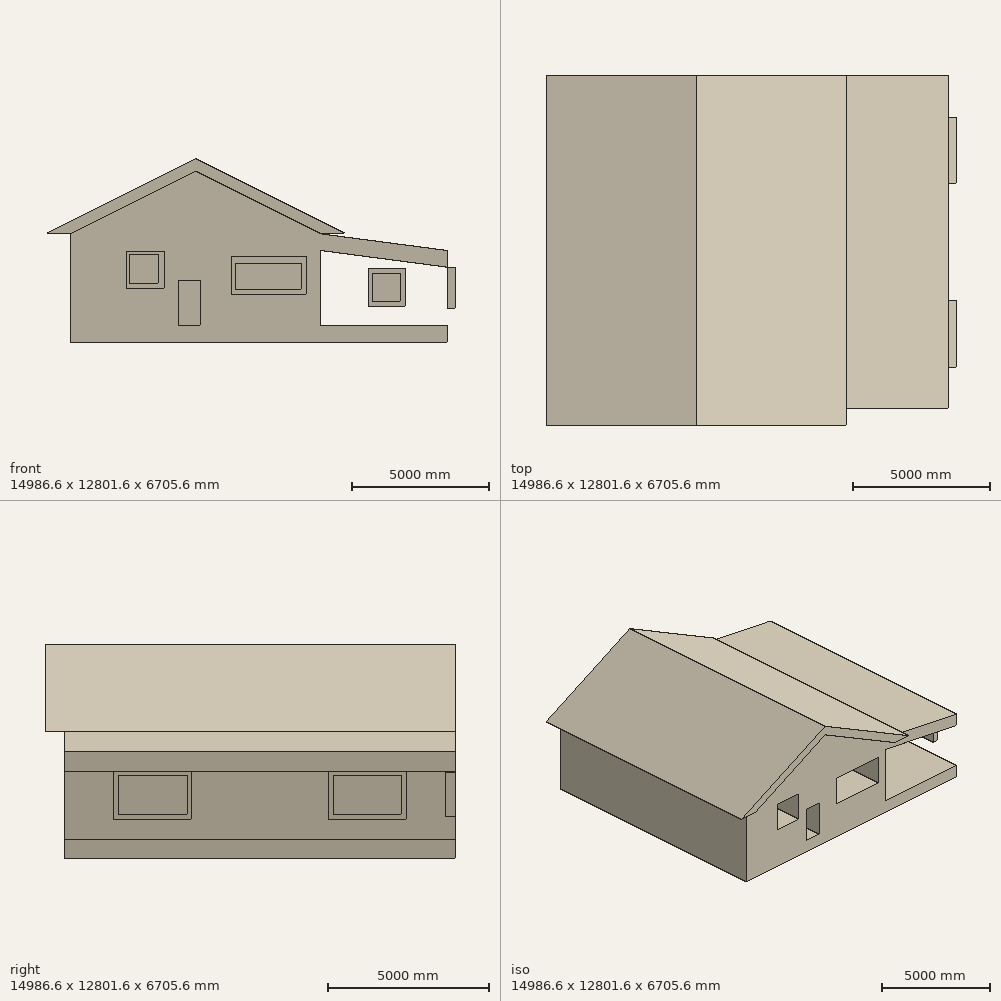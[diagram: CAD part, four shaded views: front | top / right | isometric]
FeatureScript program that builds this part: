
annotation { "Feature Type Name" : "Feature", "Feature Type Description" : "" }
export const myFeature = defineFeature(function(context is Context, id is Id, definition is map)
    precondition{}
    {
        {
            var Q0;
            Q0=qCreatedBy(makeId("Front.planeOp"),FACE);
            var sketch = newSketch(context, id + "F0", { "sketchPlane" : qUnion([Q0])});
            skLineSegment(sketch, "E0", {"start": v(0, 0) * mm, "end": v(0, 2286) * mm});
            skLineSegment(sketch, "E1", {"start": v(0, 0) * mm, "end": v(-4572, 0) * mm});
            skLineSegment(sketch, "E2", {"start": v(0, 0) * mm, "end": v(4572, 0) * mm});
            skLineSegment(sketch, "E3", {"start": v(-4572, 0) * mm, "end": v(0, 2286) * mm});
            skLineSegment(sketch, "E4", {"start": v(4572, 0) * mm, "end": v(0, 2286) * mm});
            skLineSegment(sketch, "E5", {"start": v(-4572, 0) * mm, "end": v(-5486.4, 0) * mm});
            skLineSegment(sketch, "E6", {"start": v(4572, 0) * mm, "end": v(5486.4, 0) * mm});
            skLineSegment(sketch, "E7", {"start": v(-5486.4, 0) * mm, "end": v(0, 2743.2) * mm});
            skLineSegment(sketch, "E8", {"start": v(5486.4, 0) * mm, "end": v(0, 2743.2) * mm});
            skLineSegment(sketch, "E9", {"start": v(0, 2286) * mm, "end": v(0, 2743.2) * mm});
            skLineSegment(sketch, "E10", {"start": v(-4572, 0) * mm, "end": v(-4572, -3352.8) * mm});
            skLineSegment(sketch, "E11", {"start": v(-4572, -3352.8) * mm, "end": v(4623.43, -3352.8) * mm});
            skLineSegment(sketch, "E12", {"start": v(-4572, -3352.8) * mm, "end": v(-4572, -3962.4) * mm});
            skLineSegment(sketch, "E13", {"start": v(-4572, -3962.4) * mm, "end": v(4623.43, -3962.4) * mm});
            skLineSegment(sketch, "E14", {"start": v(4572, 0) * mm, "end": v(4572, -3352.8) * mm});
            skLineSegment(sketch, "E15", {"start": v(4623.43, -3962.4) * mm, "end": v(9195.43, -3962.4) * mm});
            skLineSegment(sketch, "E16", {"start": v(4623.43, -3352.8) * mm, "end": v(9195.43, -3352.8) * mm});
            skLineSegment(sketch, "E17", {"start": v(9195.43, -3352.8) * mm, "end": v(9195.43, -609.6) * mm});
            skLineSegment(sketch, "E18", {"start": v(9195.43, -3352.8) * mm, "end": v(9195.43, -3962.4) * mm});
            skLineSegment(sketch, "E19", {"start": v(4623.43, -3352.8) * mm, "end": v(4623.43, -3962.4) * mm});
            skLineSegment(sketch, "E20", {"start": v(4572, 0) * mm, "end": v(9195.43, -609.6) * mm});
            skLineSegment(sketch, "E21", {"start": v(4572, -609.6) * mm, "end": v(4572, 0) * mm});
            skLineSegment(sketch, "E22", {"start": v(9195.43, -1219.2) * mm, "end": v(9195.43, -609.6) * mm});
            skLineSegment(sketch, "E23", {"start": v(4572, -609.6) * mm, "end": v(9195.43, -1219.2) * mm});
            skLineSegment(sketch, "E24", {"start": v(1327.2, -837.67) * mm, "end": v(1327.2, -2209.27) * mm});
            skLineSegment(sketch, "E25", {"start": v(1327.2, -2209.27) * mm, "end": v(4070.4, -2209.27) * mm});
            skLineSegment(sketch, "E26", {"start": v(4070.4, -2209.27) * mm, "end": v(4070.4, -837.67) * mm});
            skLineSegment(sketch, "E27", {"start": v(4070.4, -837.67) * mm, "end": v(1327.2, -837.67) * mm});
            skLineSegment(sketch, "E28.bottom", {"start": v(-2513.93, -640.84) * mm, "end": v(-1142.33, -640.84) * mm});
            skLineSegment(sketch, "E28.top", {"start": v(-2513.93, -2012.44) * mm, "end": v(-1142.33, -2012.44) * mm});
            skLineSegment(sketch, "E28.left", {"start": v(-2513.93, -640.84) * mm, "end": v(-2513.93, -2012.44) * mm});
            skLineSegment(sketch, "E28.right", {"start": v(-1142.33, -640.84) * mm, "end": v(-1142.33, -2012.44) * mm});
            skLineSegment(sketch, "E29.bottom", {"start": v(-2407.47, -765.33) * mm, "end": v(-1340.67, -765.33) * mm});
            skLineSegment(sketch, "E29.top", {"start": v(-2407.47, -1832.13) * mm, "end": v(-1340.67, -1832.13) * mm});
            skLineSegment(sketch, "E29.left", {"start": v(-2407.47, -765.33) * mm, "end": v(-2407.47, -1832.13) * mm});
            skLineSegment(sketch, "E29.right", {"start": v(-1340.67, -765.33) * mm, "end": v(-1340.67, -1832.13) * mm});
            skLineSegment(sketch, "E30.bottom", {"start": v(1472.1, -1092.88) * mm, "end": v(3888.2, -1092.88) * mm});
            skLineSegment(sketch, "E30.top", {"start": v(1472.1, -2030.47) * mm, "end": v(3888.2, -2030.47) * mm});
            skLineSegment(sketch, "E30.left", {"start": v(1472.1, -1092.88) * mm, "end": v(1472.1, -2030.47) * mm});
            skLineSegment(sketch, "E30.right", {"start": v(3888.2, -1092.88) * mm, "end": v(3888.2, -2030.47) * mm});
            skLineSegment(sketch, "E31.bottom", {"start": v(6303.03, -1271.91) * mm, "end": v(7674.63, -1271.91) * mm});
            skLineSegment(sketch, "E31.top", {"start": v(6303.03, -2643.51) * mm, "end": v(7674.63, -2643.51) * mm});
            skLineSegment(sketch, "E31.left", {"start": v(6303.03, -1271.91) * mm, "end": v(6303.03, -2643.51) * mm});
            skLineSegment(sketch, "E31.right", {"start": v(7674.63, -1271.91) * mm, "end": v(7674.63, -2643.51) * mm});
            skLineSegment(sketch, "E32.bottom", {"start": v(6466.58, -1453.5) * mm, "end": v(7494.32, -1453.5) * mm});
            skLineSegment(sketch, "E32.top", {"start": v(6466.58, -2463.2) * mm, "end": v(7494.32, -2463.2) * mm});
            skLineSegment(sketch, "E32.left", {"start": v(6466.58, -1453.5) * mm, "end": v(6466.58, -2463.2) * mm});
            skLineSegment(sketch, "E32.right", {"start": v(7494.32, -1453.5) * mm, "end": v(7494.32, -2463.2) * mm});
            skLineSegment(sketch, "E33.bottom", {"start": v(-631.5, -1709.5) * mm, "end": v(191.74, -1709.5) * mm});
            skLineSegment(sketch, "E33.top", {"start": v(-631.5, -3352.8) * mm, "end": v(191.74, -3352.8) * mm});
            skLineSegment(sketch, "E33.left", {"start": v(-631.5, -1709.5) * mm, "end": v(-631.5, -3352.8) * mm});
            skLineSegment(sketch, "E33.right", {"start": v(191.74, -1709.5) * mm, "end": v(191.74, -3352.8) * mm});
            skLineSegment(sketch, "E34.bottom", {"start": v(-469.54, -1857.95) * mm, "end": v(25.71, -1857.95) * mm});
            skLineSegment(sketch, "E34.top", {"start": v(-469.54, -3352.8) * mm, "end": v(25.71, -3352.8) * mm});
            skLineSegment(sketch, "E34.left", {"start": v(-469.54, -1857.95) * mm, "end": v(-469.54, -3352.8) * mm});
            skLineSegment(sketch, "E34.right", {"start": v(25.71, -1857.95) * mm, "end": v(25.71, -3352.8) * mm});
            skSolve(sketch);
        }
        {
            var Q0;
            Q0=makeQuery(id+"F0.imprint","IMPRINT",FACE,{"disambiguationData":[TD([[makeQuery(id+"F0.imprint","IMPRINT",EDGE,{"derivedFrom":sQuery(id+"F0.wireOp",EDGE,"E4")}),-1.0]])]});
            var Q1;
            Q1=makeQuery(id+"F0.imprint","IMPRINT",FACE,{"disambiguationData":[TD([[makeQuery(id+"F0.imprint","IMPRINT",EDGE,{"derivedFrom":sQuery(id+"F0.wireOp",EDGE,"E3")}),1.0]])]});
            extrude(context, id + "F1", {"entities" : qUnion([Q0, Q1]), "depth" : 12801.6 * mm, "offsetDistance" : 30.48 * mm});
        }
        {
            var Q0;
            Q0=makeQuery(id+"F0.imprint","IMPRINT",FACE,{"disambiguationData":[TD([[makeQuery(id+"F0.imprint","IMPRINT",EDGE,{"derivedFrom":sQuery(id+"F0.wireOp",EDGE,"E0")}),1.0]])]});
            var Q1;
            Q1=makeQuery(id+"F0.imprint","IMPRINT",FACE,{"disambiguationData":[TD([[makeQuery(id+"F0.imprint","IMPRINT",EDGE,{"derivedFrom":sQuery(id+"F0.wireOp",EDGE,"E0")}),-1.0]])]});
            var Q2;
            Q2=makeQuery(id+"F0.imprint","IMPRINT",FACE,{"disambiguationData":[TD([[makeQuery(id+"F0.imprint","IMPRINT",EDGE,{"derivedFrom":sQuery(id+"F0.wireOp",EDGE,"E1")}),1.0]])]});
            var Q3;
            {var subQ0=sQuery(id+"F0.wireOp",EDGE,"E12");Q3=makeQuery(id+"F0.imprint","IMPRINT",FACE,{"disambiguationData":[TD([[makeQuery(id+"F0.imprint","IMPRINT",EDGE,{"derivedFrom":subQ0}),1.0]])]});}
            var Q4;
            Q4=makeQuery(id+"F0.imprint","IMPRINT",FACE,{"disambiguationData":[TD([[makeQuery(id+"F0.imprint","IMPRINT",EDGE,{"derivedFrom":sQuery(id+"F0.wireOp",EDGE,"E15")}),1.0]])]});
            var Q5;
            {var subQ0=sQuery(id+"F0.wireOp",EDGE,"E14");Q5=makeQuery(id+"F0.imprint","IMPRINT",FACE,{"disambiguationData":[TD([[makeQuery(id+"F0.imprint","IMPRINT",EDGE,{"derivedFrom":subQ0}),1.0]])]});}
            var Q6;
            Q6=makeQuery(id+"F0.imprint","IMPRINT",FACE,{"disambiguationData":[TD([[makeQuery(id+"F0.imprint","IMPRINT",EDGE,{"derivedFrom":sQuery(id+"F0.wireOp",EDGE,"E20")}),-1.0]])]});
            extrude(context, id + "F2", {"entities" : qUnion([Q0, Q1, Q2, Q3, Q4, Q5, Q6]), "operationType" : NewBodyOperationType.ADD, "depth" : 12192 * mm, "offsetDistance" : 30.48 * mm});
        }
        {
            var Q0;
            Q0=makeQuery(id+"F0.imprint","IMPRINT",FACE,{"disambiguationData":[TD([[makeQuery(id+"F0.imprint","IMPRINT",EDGE,{"derivedFrom":sQuery(id+"F0.wireOp",EDGE,"E29.bottom")}),-1.0]])]});
            var Q1;
            Q1=makeQuery(id+"F0.imprint","IMPRINT",FACE,{"disambiguationData":[TD([[makeQuery(id+"F0.imprint","IMPRINT",EDGE,{"derivedFrom":sQuery(id+"F0.wireOp",EDGE,"E32.bottom")}),-1.0]])]});
            var Q2;
            Q2=makeQuery(id+"F0.imprint","IMPRINT",FACE,{"disambiguationData":[TD([[makeQuery(id+"F0.imprint","IMPRINT",EDGE,{"derivedFrom":sQuery(id+"F0.wireOp",EDGE,"E30.bottom")}),-1.0]])]});
            extrude(context, id + "F3", {"entities" : qUnion([Q0, Q1, Q2]), "depth" : 30.48 * mm, "offsetDistance" : 30.48 * mm});
        }
        {
            var Q0;
            Q0=makeQuery(id+"F2.opExtrude","SWEPT_FACE",FACE,{"disambiguationData":[OSD([sQuery(id+"F0.wireOp",EDGE,"E17"),sQuery(id+"F0.wireOp",EDGE,"E18"),sQuery(id+"F0.wireOp",EDGE,"E22")])]});
            var sketch = newSketch(context, id + "F4", { "sketchPlane" : qUnion([Q0])});
            skLineSegment(sketch, "E35.bottom", {"start": v(-10668, -1219.2) * mm, "end": v(-8229.6, -1219.2) * mm});
            skLineSegment(sketch, "E35.top", {"start": v(-10668, -2743.2) * mm, "end": v(-8229.6, -2743.2) * mm});
            skLineSegment(sketch, "E35.left", {"start": v(-10668, -1219.2) * mm, "end": v(-10668, -2743.2) * mm});
            skLineSegment(sketch, "E35.right", {"start": v(-8229.6, -1219.2) * mm, "end": v(-8229.6, -2743.2) * mm});
            skLineSegment(sketch, "E36.bottom", {"start": v(-10515.6, -1371.6) * mm, "end": v(-8382, -1371.6) * mm});
            skLineSegment(sketch, "E36.top", {"start": v(-10515.6, -2590.8) * mm, "end": v(-8382, -2590.8) * mm});
            skLineSegment(sketch, "E36.left", {"start": v(-10515.6, -1371.6) * mm, "end": v(-10515.6, -2590.8) * mm});
            skLineSegment(sketch, "E36.right", {"start": v(-8382, -1371.6) * mm, "end": v(-8382, -2590.8) * mm});
            skLineSegment(sketch, "E37.bottom", {"start": v(-3962.4, -1219.2) * mm, "end": v(-1524, -1219.2) * mm});
            skLineSegment(sketch, "E37.top", {"start": v(-3962.4, -2743.2) * mm, "end": v(-1524, -2743.2) * mm});
            skLineSegment(sketch, "E37.left", {"start": v(-3962.4, -1219.2) * mm, "end": v(-3962.4, -2743.2) * mm});
            skLineSegment(sketch, "E37.right", {"start": v(-1524, -1219.2) * mm, "end": v(-1524, -2743.2) * mm});
            skLineSegment(sketch, "E38.bottom", {"start": v(-3810, -1371.6) * mm, "end": v(-1676.4, -1371.6) * mm});
            skLineSegment(sketch, "E38.top", {"start": v(-3810, -2590.8) * mm, "end": v(-1676.4, -2590.8) * mm});
            skLineSegment(sketch, "E38.left", {"start": v(-3810, -1371.6) * mm, "end": v(-3810, -2590.8) * mm});
            skLineSegment(sketch, "E38.right", {"start": v(-1676.4, -1371.6) * mm, "end": v(-1676.4, -2590.8) * mm});
            skSolve(sketch);
        }
        {
            var Q0;
            Q0=makeQuery(id+"F4.imprint","IMPRINT",FACE,{"disambiguationData":[TD([[makeQuery(id+"F4.imprint","IMPRINT",EDGE,{"derivedFrom":sQuery(id+"F4.wireOp",EDGE,"E36.bottom")}),-1.0]])]});
            var Q1;
            Q1=makeQuery(id+"F4.imprint","IMPRINT",FACE,{"disambiguationData":[TD([[makeQuery(id+"F4.imprint","IMPRINT",EDGE,{"derivedFrom":sQuery(id+"F4.wireOp",EDGE,"E38.bottom")}),-1.0]])]});
            extrude(context, id + "F5", {"entities" : qUnion([Q0, Q1]), "operationType" : NewBodyOperationType.ADD, "depth" : 152.4 * mm, "offsetDistance" : 30.48 * mm});
        }
        {
            var Q0;
            Q0=makeQuery(id+"F4.imprint","IMPRINT",FACE,{"disambiguationData":[TD([[makeQuery(id+"F4.imprint","IMPRINT",EDGE,{"derivedFrom":sQuery(id+"F4.wireOp",EDGE,"E35.bottom")}),-1.0]])]});
            var Q1;
            Q1=makeQuery(id+"F4.imprint","IMPRINT",FACE,{"disambiguationData":[TD([[makeQuery(id+"F4.imprint","IMPRINT",EDGE,{"derivedFrom":sQuery(id+"F4.wireOp",EDGE,"E37.bottom")}),-1.0]])]});
            extrude(context, id + "F6", {"entities" : qUnion([Q0, Q1]), "operationType" : NewBodyOperationType.ADD, "depth" : 304.8 * mm, "offsetDistance" : 30.48 * mm});
        }
        {
            var Q0;
            Q0=makeQuery(id+"F0.imprint","IMPRINT",FACE,{"disambiguationData":[TD([[makeQuery(id+"F0.imprint","IMPRINT",EDGE,{"derivedFrom":sQuery(id+"F0.wireOp",EDGE,"E28.bottom")}),-1.0]])]});
            var Q1;
            Q1=makeQuery(id+"F0.imprint","IMPRINT",FACE,{"disambiguationData":[TD([[makeQuery(id+"F0.imprint","IMPRINT",EDGE,{"derivedFrom":sQuery(id+"F0.wireOp",EDGE,"E24")}),1.0]])]});
            var Q2;
            Q2=makeQuery(id+"F0.imprint","IMPRINT",FACE,{"disambiguationData":[TD([[makeQuery(id+"F0.imprint","IMPRINT",EDGE,{"derivedFrom":sQuery(id+"F0.wireOp",EDGE,"E31.bottom")}),-1.0]])]});
            extrude(context, id + "F7", {"entities" : qUnion([Q0, Q1, Q2]), "depth" : 304.8 * mm, "offsetDistance" : 30.48 * mm});
        }
        {
            var Q0;
            Q0=makeQuery(id+"F0.imprint","IMPRINT",FACE,{"disambiguationData":[TD([[makeQuery(id+"F0.imprint","IMPRINT",EDGE,{"derivedFrom":sQuery(id+"F0.wireOp",EDGE,"E33.bottom")}),-1.0]])]});
            var Q1;
            Q1=makeQuery(id+"F0.imprint","IMPRINT",FACE,{"disambiguationData":[TD([[makeQuery(id+"F0.imprint","IMPRINT",EDGE,{"derivedFrom":sQuery(id+"F0.wireOp",EDGE,"E34.bottom")}),-1.0]])]});
            extrude(context, id + "F8", {"entities" : qUnion([Q0, Q1]), "operationType" : NewBodyOperationType.ADD, "depth" : 30.48 * mm, "offsetDistance" : 30.48 * mm});
        }
    });
